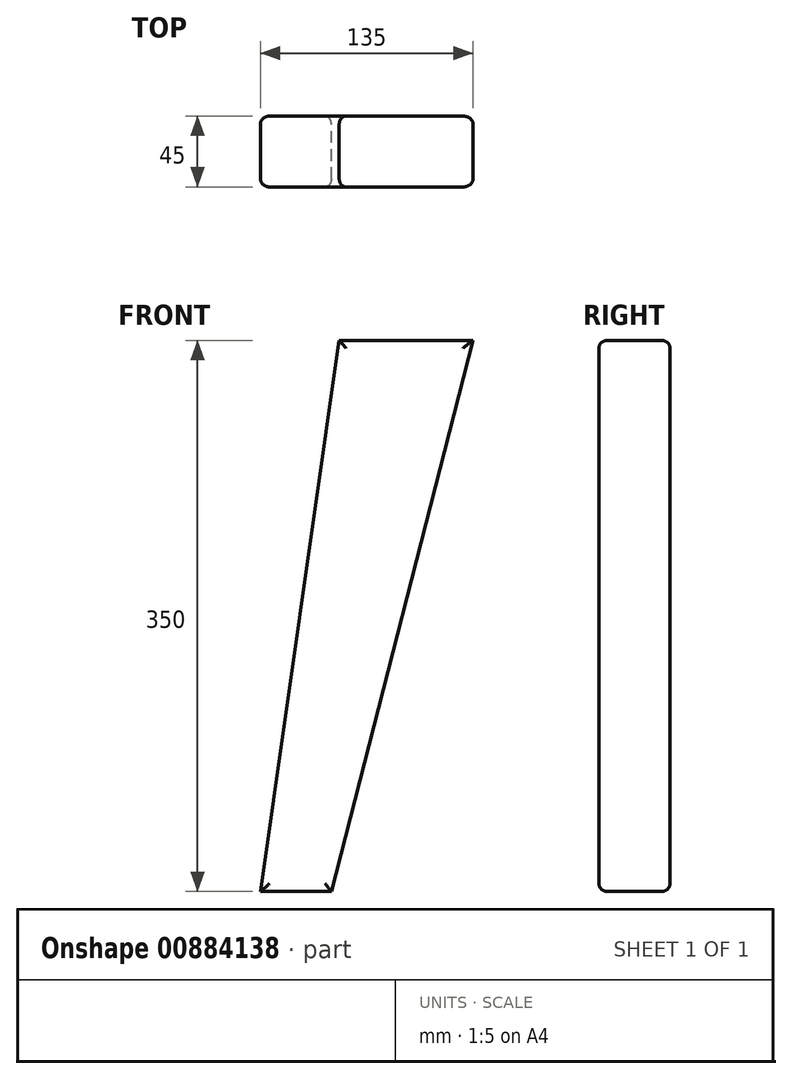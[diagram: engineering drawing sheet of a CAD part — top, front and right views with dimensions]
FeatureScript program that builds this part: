
annotation { "Feature Type Name" : "Feature", "Feature Type Description" : "" }
export const myFeature = defineFeature(function(context is Context, id is Id, definition is map)
    precondition{}
    {
        {
            var Q0;
            Q0=qCreatedBy(makeId("Front.planeOp"),FACE);
            var sketch = newSketch(context, id + "F0", { "sketchPlane" : qUnion([Q0])});
            skPoint(sketch, "E0.middle", {"position": v(0, 0) * mm});
            skLineSegment(sketch, "E1", {"start": v(-85, 175) * mm, "end": v(-135, -175) * mm});
            skLineSegment(sketch, "E2", {"start": v(-135, -175) * mm, "end": v(-90, -175) * mm});
            skLineSegment(sketch, "E3", {"start": v(-90, -175) * mm, "end": v(-135, -175) * mm});
            skLineSegment(sketch, "E4", {"start": v(-85, 175) * mm, "end": v(0, 175) * mm});
            skLineSegment(sketch, "E5", {"start": v(0, 175) * mm, "end": v(-90, -175) * mm});
            skSolve(sketch);
        }
        {
            var Q0;
            Q0 = qSketchRegion(id + "F0", true);
            extrude(context, id + "F1", {"entities" : qUnion([Q0]), "depth" : 45 * mm, "offsetDistance" : 25 * mm});
        }
        {
            var Q0;
            Q0=makeQuery(id+"F1.opExtrude","CAP_FACE",FACE,{"disambiguationData":[OSD([sQuery(id+"F0.wireOp",EDGE,"E1"),sQuery(id+"F0.wireOp",EDGE,"E3"),sQuery(id+"F0.wireOp",EDGE,"E4"),sQuery(id+"F0.wireOp",EDGE,"E5")])],"isStart":false});
            var Q1;
            Q1=makeQuery(id+"F1.opExtrude","CAP_FACE",FACE,{"disambiguationData":[OSD([sQuery(id+"F0.wireOp",EDGE,"E1"),sQuery(id+"F0.wireOp",EDGE,"E3"),sQuery(id+"F0.wireOp",EDGE,"E4"),sQuery(id+"F0.wireOp",EDGE,"E5")])],"isStart":true});
            fillet(context, id + "F2", {"entities" : qUnion([Q0, Q1]), "radius" : 5 * mm, "tangentPropagation" : true, "allowEdgeOverflow" : false});
        }
    });
